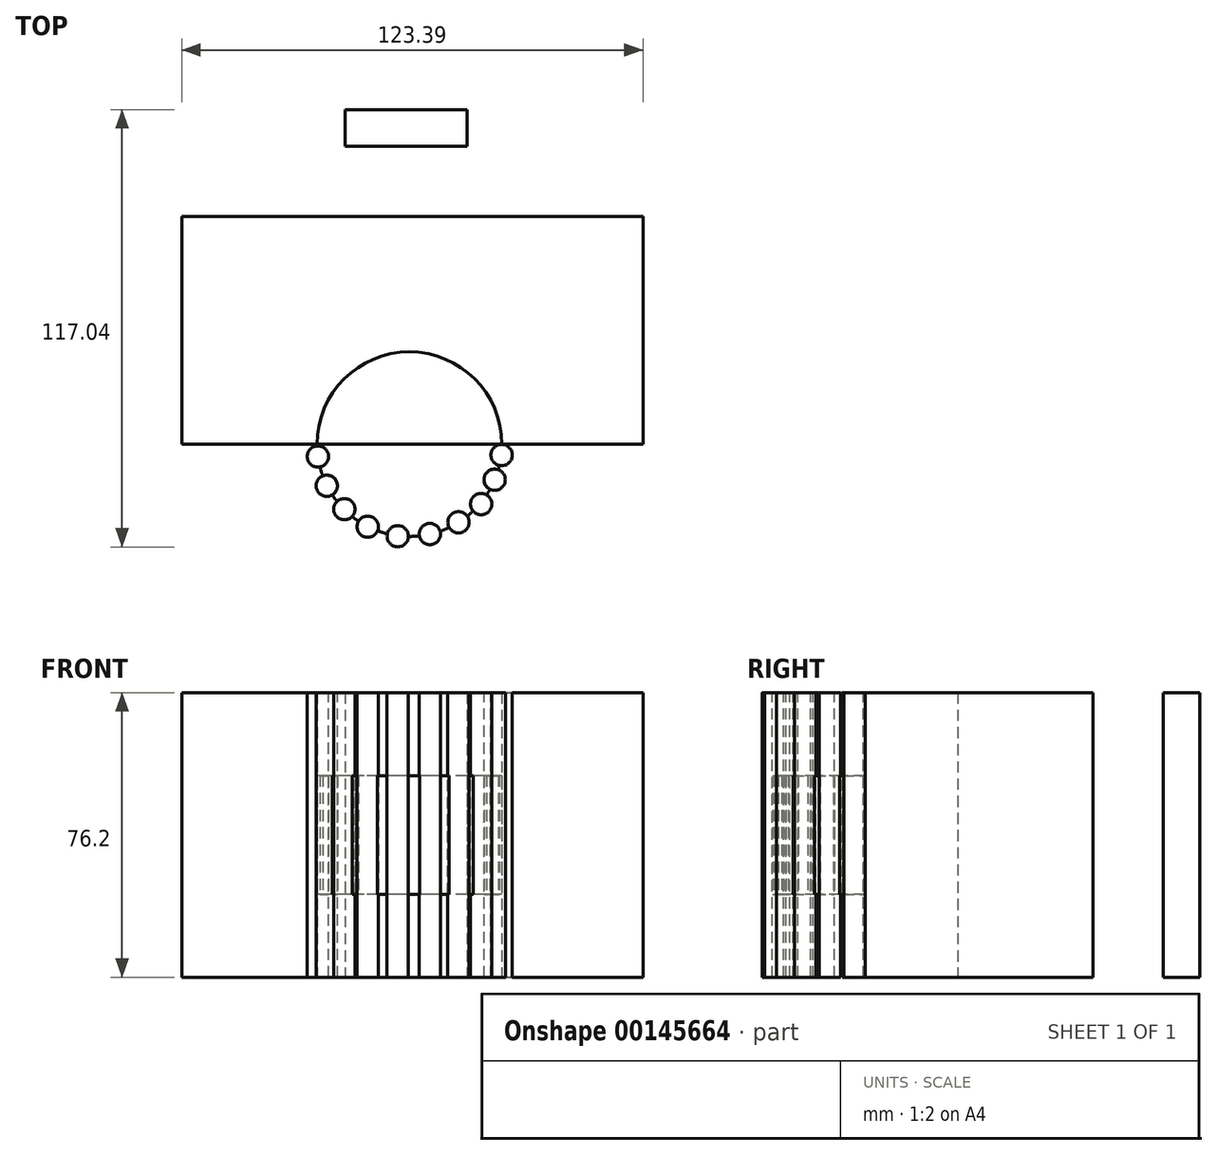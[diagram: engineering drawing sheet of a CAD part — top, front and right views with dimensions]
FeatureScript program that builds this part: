
annotation { "Feature Type Name" : "Feature", "Feature Type Description" : "" }
export const myFeature = defineFeature(function(context is Context, id is Id, definition is map)
    precondition{}
    {
        {
            var Q0;
            Q0=qCreatedBy(makeId("Top.planeOp"),FACE);
            var sketch = newSketch(context, id + "F0", { "sketchPlane" : qUnion([Q0])});
            skLineSegment(sketch, "E0.bottom", {"start": v(-60.91, 27.71) * mm, "end": v(62.48, 27.71) * mm});
            skLineSegment(sketch, "E0.top", {"start": v(-60.91, -33.23) * mm, "end": v(62.48, -33.23) * mm});
            skLineSegment(sketch, "E0.left", {"start": v(-60.91, 27.71) * mm, "end": v(-60.91, -33.23) * mm});
            skLineSegment(sketch, "E0.right", {"start": v(62.48, 27.71) * mm, "end": v(62.48, -33.23) * mm});
            skCircle(sketch, "E1", {"center": v(0, -33.23) * mm, "radius": 24.72 * mm});
            skLineSegment(sketch, "E2.bottom", {"start": v(-17.24, 27.71) * mm, "end": v(15.47, 27.71) * mm});
            skLineSegment(sketch, "E2.top", {"start": v(-17.24, 46.52) * mm, "end": v(15.47, 46.52) * mm});
            skLineSegment(sketch, "E2.left", {"start": v(-17.24, 27.71) * mm, "end": v(-17.24, 46.52) * mm});
            skLineSegment(sketch, "E2.right", {"start": v(15.47, 27.71) * mm, "end": v(15.47, 46.52) * mm});
            skLineSegment(sketch, "E3.bottom", {"start": v(15.47, 46.52) * mm, "end": v(15.47, 46.52) * mm});
            skLineSegment(sketch, "E3.top", {"start": v(15.47, 55.33) * mm, "end": v(15.47, 55.33) * mm});
            skLineSegment(sketch, "E3.left", {"start": v(15.47, 46.52) * mm, "end": v(15.47, 55.33) * mm});
            skLineSegment(sketch, "E3.right", {"start": v(15.47, 46.52) * mm, "end": v(15.47, 55.33) * mm});
            skLineSegment(sketch, "E4.bottom", {"start": v(-17.24, 46.52) * mm, "end": v(-17.24, 46.52) * mm});
            skLineSegment(sketch, "E4.top", {"start": v(-17.24, 56.31) * mm, "end": v(-17.24, 56.31) * mm});
            skLineSegment(sketch, "E4.left", {"start": v(-17.24, 46.52) * mm, "end": v(-17.24, 56.31) * mm});
            skLineSegment(sketch, "E4.right", {"start": v(-17.24, 46.52) * mm, "end": v(-17.24, 56.31) * mm});
            skLineSegment(sketch, "E5.bottom", {"start": v(-17.24, 56.31) * mm, "end": v(15.47, 56.31) * mm});
            skLineSegment(sketch, "E5.left", {"start": v(-17.24, 56.31) * mm, "end": v(-17.24, 46.52) * mm});
            skLineSegment(sketch, "E5.right", {"start": v(15.47, 56.31) * mm, "end": v(15.47, 46.52) * mm});
            skSolve(sketch);
        }
        {
            var Q0;
            {var subQ4=sQuery(id+"F0.wireOp",EDGE,"E0.left");Q0=makeQuery(id+"F0.imprint","IMPRINT",FACE,{"disambiguationData":[TD([[makeQuery(id+"F0.imprint","IMPRINT",EDGE,{"derivedFrom":subQ4}),1.0]])]});}
            var Q1;
            {var subQ0=sQuery(id+"F0.wireOp",EDGE,"E1");var subQ1=sQuery(id+"F0.wireOp",EDGE,"E0.top");var subQ2=makeQuery(id+"F0.imprint","INTERSECT",VERTEX,{"disambiguationData":[OD(0.0)],"derivedFrom":[subQ1,subQ0]});Q1=makeQuery(id+"F0.imprint","IMPRINT",FACE,{"disambiguationData":[TD([[makeQuery(id+"F0.imprint","IMPRINT",EDGE,{"disambiguationData":[TD([[subQ2,-1.0]])],"derivedFrom":subQ1}),-1.0]])]});}
            var Q2;
            Q2=makeQuery(id+"F0.imprint","IMPRINT",FACE,{"disambiguationData":[TD([[makeQuery(id+"F0.imprint","IMPRINT",EDGE,{"derivedFrom":sQuery(id+"F0.wireOp",EDGE,"E2.bottom")}),1.0]])]});
            var Q3;
            {var subQ0=sQuery(id+"F0.wireOp",EDGE,"E5.bottom");Q3=makeQuery(id+"F0.imprint","IMPRINT",FACE,{"disambiguationData":[TD([[makeQuery(id+"F0.imprint","IMPRINT",EDGE,{"derivedFrom":subQ0}),-1.0]])]});}
            var Q4;
            {var subQ0=sQuery(id+"F0.wireOp",EDGE,"E1");var subQ1=sQuery(id+"F0.wireOp",EDGE,"E0.top");var subQ2=makeQuery(id+"F0.imprint","INTERSECT",VERTEX,{"disambiguationData":[OD(0.0)],"derivedFrom":[subQ1,subQ0]});Q4=makeQuery(id+"F0.imprint","IMPRINT",FACE,{"disambiguationData":[TD([[makeQuery(id+"F0.imprint","IMPRINT",EDGE,{"disambiguationData":[TD([[subQ2,-1.0]])],"derivedFrom":subQ1}),1.0]])]});}
            extrude(context, id + "F1", {"entities" : qUnion([Q0, Q1, Q2, Q3, Q4]), "depth" : 76.2 * mm});
        }
        {
            var Q0;
            Q0=makeQuery(id+"F1.opExtrude","CAP_FACE",FACE,{"disambiguationData":[OSD([sQuery(id+"F0.wireOp",EDGE,"E0.bottom"),sQuery(id+"F0.wireOp",EDGE,"E0.top"),sQuery(id+"F0.wireOp",EDGE,"E0.left"),sQuery(id+"F0.wireOp",EDGE,"E0.right"),sQuery(id+"F0.wireOp",EDGE,"E1"),sQuery(id+"F0.wireOp",EDGE,"E2.left"),sQuery(id+"F0.wireOp",EDGE,"E2.right"),sQuery(id+"F0.wireOp",EDGE,"E5.bottom"),sQuery(id+"F0.wireOp",EDGE,"E5.left"),sQuery(id+"F0.wireOp",EDGE,"E5.right")])],"isStart":false});
            var sketch = newSketch(context, id + "F2", { "sketchPlane" : qUnion([Q0])});
            skCircle(sketch, "E6", {"center": v(-24.5, -36.53) * mm, "radius": 2.85 * mm});
            skCircle(sketch, "E7", {"center": v(-22.13, -44.36) * mm, "radius": 2.85 * mm});
            skCircle(sketch, "E8", {"center": v(-17.43, -50.63) * mm, "radius": 2.85 * mm});
            skCircle(sketch, "E9", {"center": v(-11.16, -55.33) * mm, "radius": 2.85 * mm});
            skCircle(sketch, "E10", {"center": v(-3.13, -57.88) * mm, "radius": 2.85 * mm});
            skCircle(sketch, "E11", {"center": v(5.48, -57.3) * mm, "radius": 2.85 * mm});
            skCircle(sketch, "E12", {"center": v(13.12, -54.16) * mm, "radius": 2.85 * mm});
            skCircle(sketch, "E13", {"center": v(19.2, -49.26) * mm, "radius": 2.85 * mm});
            skCircle(sketch, "E14", {"center": v(22.81, -42.74) * mm, "radius": 2.85 * mm});
            skCircle(sketch, "E15", {"center": v(24.68, -36.14) * mm, "radius": 2.85 * mm});
            skSolve(sketch);
        }
        {
            var Q0;
            Q0 = qSketchRegion(id + "F2", true);
            extrude(context, id + "F3", {"entities" : qUnion([Q0]), "operationType" : NewBodyOperationType.ADD, "oppositeDirection" : true, "depth" : 76.2 * mm});
        }
        {
            var Q0;
            Q0=qCreatedBy(makeId("Top.planeOp"),FACE);
            cPlane(context, id + "F4", {"entities" : qUnion([Q0]), "cplaneType" : CPlaneType.OFFSET, "offset" : 38.1 * mm, "width" : 152.4 * mm, "height" : 152.4 * mm});
        }
        {
            var Q0;
            Q0=qCreatedBy(id+"F4.planeOp",FACE);
            var sketch = newSketch(context, id + "F5", { "sketchPlane" : qUnion([Q0])});
            skArc(sketch, "E16.0", {"start": v(-23.95, -39.33) * mm, "mid": v(-23.61, -40.54) * mm, "end": v(-23.21, -41.72) * mm});
            skArc(sketch, "E16.1", {"start": v(-20.65, -46.8) * mm, "mid": v(-20.04, -47.7) * mm, "end": v(-19.39, -48.55) * mm});
            skArc(sketch, "E16.2", {"start": v(-15.36, -52.6) * mm, "mid": v(-14.5, -53.24) * mm, "end": v(-13.6, -53.86) * mm});
            skArc(sketch, "E16.3", {"start": v(-8.53, -56.43) * mm, "mid": v(-7.23, -56.86) * mm, "end": v(-5.91, -57.23) * mm});
            skArc(sketch, "E16.4", {"start": v(-0.28, -57.94) * mm, "mid": v(1.2, -57.91) * mm, "end": v(2.68, -57.8) * mm});
            skArc(sketch, "E16.5", {"start": v(8.23, -56.53) * mm, "mid": v(9.44, -56.07) * mm, "end": v(10.63, -55.54) * mm});
            skArc(sketch, "E16.6", {"start": v(15.46, -52.51) * mm, "mid": v(16.26, -51.84) * mm, "end": v(17.04, -51.13) * mm});
            skArc(sketch, "E16.7", {"start": v(20.65, -46.8) * mm, "mid": v(21.12, -46.06) * mm, "end": v(21.56, -45.3) * mm});
            skArc(sketch, "E16.8", {"start": v(23.76, -40.05) * mm, "mid": v(23.91, -39.48) * mm, "end": v(24.05, -38.92) * mm});
            skArc(sketch, "E16.9", {"start": v(-24.72, -33.23) * mm, "mid": v(-24.72, -33.46) * mm, "end": v(-24.71, -33.68) * mm});
            skArc(sketch, "E17.4", {"start": v(-5.91, -57.23) * mm, "mid": v(-3.5, -60.7) * mm, "end": v(-0.28, -57.94) * mm, "construction": true});
            skArc(sketch, "E17.5", {"start": v(2.68, -57.8) * mm, "mid": v(6.12, -60.07) * mm, "end": v(8.23, -56.53) * mm, "construction": true});
            skArc(sketch, "E17.6", {"start": v(10.63, -55.54) * mm, "mid": v(14.64, -56.57) * mm, "end": v(15.46, -52.51) * mm, "construction": true});
            skArc(sketch, "E17.7", {"start": v(17.04, -51.13) * mm, "mid": v(21.38, -51.09) * mm, "end": v(20.65, -46.8) * mm, "construction": true});
            skArc(sketch, "E17.8", {"start": v(21.56, -45.3) * mm, "mid": v(25.45, -43.84) * mm, "end": v(23.76, -40.05) * mm, "construction": true});
            skArc(sketch, "E17.9", {"start": v(24.05, -38.92) * mm, "mid": v(27.51, -36.47) * mm, "end": v(24.72, -33.28) * mm, "construction": true});
            skArc(sketch, "E18", {"start": v(24.72, -33.28) * mm, "mid": v(21.84, -35.8) * mm, "end": v(24.05, -38.92) * mm});
            skArc(sketch, "E19", {"start": v(23.76, -40.05) * mm, "mid": v(20.18, -41.64) * mm, "end": v(21.56, -45.3) * mm});
            skArc(sketch, "E20", {"start": v(20.65, -46.8) * mm, "mid": v(17, -47.43) * mm, "end": v(17.04, -51.13) * mm});
            skArc(sketch, "E21", {"start": v(15.46, -52.51) * mm, "mid": v(11.6, -51.74) * mm, "end": v(10.63, -55.54) * mm});
            skArc(sketch, "E22", {"start": v(8.23, -56.53) * mm, "mid": v(4.85, -54.5) * mm, "end": v(2.68, -57.8) * mm});
            skArc(sketch, "E23", {"start": v(-0.28, -57.94) * mm, "mid": v(-2.77, -55.05) * mm, "end": v(-5.91, -57.23) * mm});
            skArc(sketch, "E24", {"start": v(-8.53, -56.43) * mm, "mid": v(-9.88, -52.78) * mm, "end": v(-13.6, -53.86) * mm});
            skArc(sketch, "E25", {"start": v(-15.36, -52.6) * mm, "mid": v(-15.41, -48.61) * mm, "end": v(-19.39, -48.55) * mm});
            skArc(sketch, "E26", {"start": v(-20.65, -46.8) * mm, "mid": v(-19.58, -43.08) * mm, "end": v(-23.21, -41.72) * mm});
            skArc(sketch, "E27", {"start": v(-23.95, -39.33) * mm, "mid": v(-21.67, -36.15) * mm, "end": v(-24.71, -33.68) * mm});
            skLineSegment(sketch, "E28", {"start": v(24.72, -33.28) * mm, "end": v(-24.72, -33.23) * mm});
            skSolve(sketch);
        }
        {
            var Q0;
            Q0 = qSketchRegion(id + "F5", true);
            extrude(context, id + "F6", {"entities" : qUnion([Q0]), "endBound" : BoundingType.SYMMETRIC, "depth" : 31.75 * mm});
        }
        {
            var Q0;
            Q0=makeQuery(id+"F6.opExtrude","SWEPT_BODY",BODY,{"disambiguationData":[OSD([sQuery(id+"F5.wireOp",EDGE,"E18"),sQuery(id+"F5.wireOp",EDGE,"E28")])]});
            deleteBodies(context, id + "F7", {"entities" : qUnion([Q0])});
        }
    });
